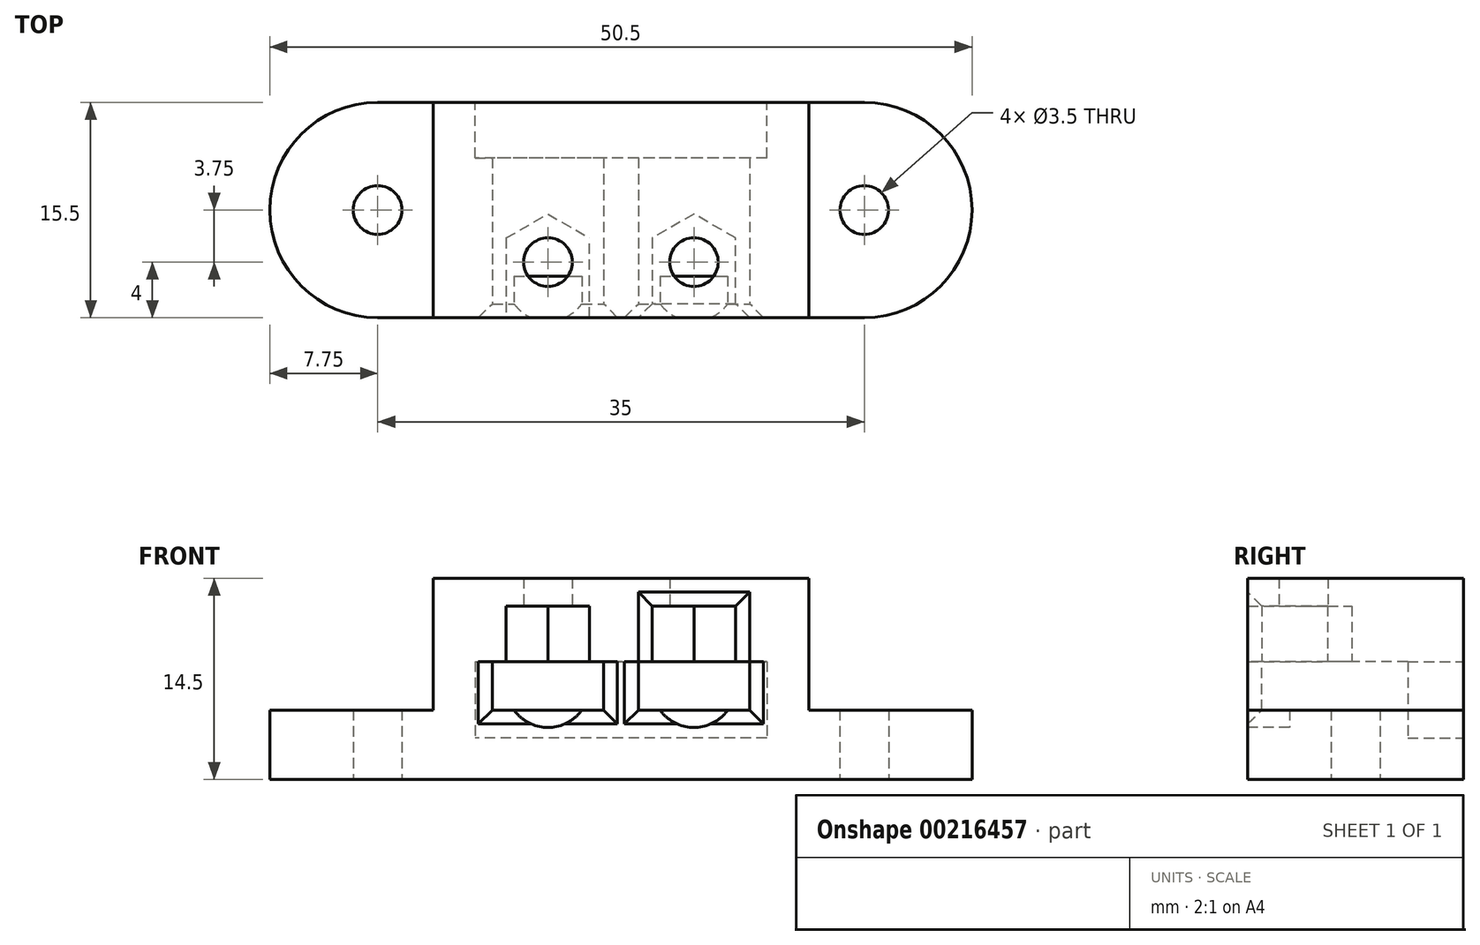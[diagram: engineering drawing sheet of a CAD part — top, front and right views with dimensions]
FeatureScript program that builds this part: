
annotation { "Feature Type Name" : "Feature", "Feature Type Description" : "" }
export const myFeature = defineFeature(function(context is Context, id is Id, definition is map)
    precondition{}
    {
        {
            var Q0;
            Q0=qCreatedBy(makeId("Top.planeOp"),FACE);
            var sketch = newSketch(context, id + "F0", { "sketchPlane" : qUnion([Q0])});
            skLineSegment(sketch, "E0", {"start": v(0, 0) * mm, "end": v(-1.25, 0) * mm});
            skLineSegment(sketch, "E1", {"start": v(-1.25, 0) * mm, "end": v(-1.25, -11.5) * mm});
            skLineSegment(sketch, "E2", {"start": v(-1.25, -11.5) * mm, "end": v(0, -11.5) * mm});
            skLineSegment(sketch, "E3", {"start": v(-5.25, 0) * mm, "end": v(-5.25, -13.93) * mm, "construction": true});
            skLineSegment(sketch, "E4.MirrorCS", {"start": v(-9.25, 0) * mm, "end": v(-9.25, -11.5) * mm});
            skLineSegment(sketch, "E5", {"start": v(-9.25, -11.5) * mm, "end": v(-10.5, -11.5) * mm});
            skLineSegment(sketch, "E6", {"start": v(-10.5, -11.5) * mm, "end": v(-10.5, 0) * mm});
            skLineSegment(sketch, "E7", {"start": v(-10.5, 0) * mm, "end": v(-9.25, 0) * mm});
            skLineSegment(sketch, "E8.MirrorCS", {"start": v(1.25, 0) * mm, "end": v(1.25, -11.5) * mm});
            skLineSegment(sketch, "E9.MirrorCS", {"start": v(1.25, -11.5) * mm, "end": v(0, -11.5) * mm});
            skLineSegment(sketch, "E10.MirrorCS", {"start": v(5.25, 0) * mm, "end": v(5.25, -13.93) * mm, "construction": true});
            skLineSegment(sketch, "E11.MirrorCS", {"start": v(9.25, -11.5) * mm, "end": v(10.5, -11.5) * mm});
            skLineSegment(sketch, "E12.MirrorCS", {"start": v(10.5, -11.5) * mm, "end": v(10.5, 0) * mm});
            skLineSegment(sketch, "E13.MirrorCS", {"start": v(10.5, 0) * mm, "end": v(9.25, 0) * mm});
            skLineSegment(sketch, "E14.MirrorCS", {"start": v(9.25, 0) * mm, "end": v(9.25, -11.5) * mm});
            skLineSegment(sketch, "E15.MirrorCS", {"start": v(0, 0) * mm, "end": v(1.25, 0) * mm});
            skSolve(sketch);
        }
        {
            var Q0;
            Q0=qSketchRegion(id+"F0",true);
            extrude(context, id + "F1", {"entities" : qUnion([Q0]), "depth" : 3.5 * mm});
        }
        {
            var Q0;
            Q0=qCreatedBy(makeId("Top.planeOp"),FACE);
            var sketch = newSketch(context, id + "F2", { "sketchPlane" : qUnion([Q0])});
            skLineSegment(sketch, "E16.bottom", {"start": v(10.5, 0) * mm, "end": v(-10.5, 0) * mm});
            skLineSegment(sketch, "E16.top", {"start": v(10.5, -11.5) * mm, "end": v(-10.5, -11.5) * mm});
            skLineSegment(sketch, "E16.left", {"start": v(10.5, 0) * mm, "end": v(10.5, -11.5) * mm});
            skLineSegment(sketch, "E16.right", {"start": v(-10.5, 0) * mm, "end": v(-10.5, -11.5) * mm});
            skSolve(sketch);
        }
        {
            var Q0;
            Q0=qSketchRegion(id+"F2",true);
            extrude(context, id + "F3", {"entities" : qUnion([Q0]), "operationType" : NewBodyOperationType.ADD, "oppositeDirection" : true, "depth" : 2 * mm});
        }
        {
            var Q0;
            Q0=qCreatedBy(makeId("Front.planeOp"),FACE);
            var sketch = newSketch(context, id + "F4", { "sketchPlane" : qUnion([Q0])});
            skLineSegment(sketch, "E17.bottom", {"start": v(-10.5, -2) * mm, "end": v(10.5, -2) * mm});
            skLineSegment(sketch, "E17.top", {"start": v(-10.5, 3.5) * mm, "end": v(10.5, 3.5) * mm});
            skLineSegment(sketch, "E17.left", {"start": v(-10.5, 3.5) * mm, "end": v(-10.5, -2) * mm});
            skLineSegment(sketch, "E17.right", {"start": v(10.5, 3.5) * mm, "end": v(10.5, -2) * mm});
            skLineSegment(sketch, "E18.bottom", {"start": v(-13.5, -5) * mm, "end": v(13.5, -5) * mm});
            skLineSegment(sketch, "E18.top", {"start": v(-13.5, 9.5) * mm, "end": v(13.5, 9.5) * mm});
            skLineSegment(sketch, "E18.left", {"start": v(-13.5, 9.5) * mm, "end": v(-13.5, -5) * mm});
            skLineSegment(sketch, "E18.right", {"start": v(13.5, 9.5) * mm, "end": v(13.5, -5) * mm});
            skPoint(sketch, "E19", {"position": v(0, -2) * mm});
            skPoint(sketch, "E20", {"position": v(0, -5) * mm});
            skPoint(sketch, "E21", {"position": v(10.5, 0.75) * mm});
            skSolve(sketch);
        }
        {
            var Q0;
            Q0 = qSketchRegion(id + "F4", true);
            var Q1;
            Q1=makeQuery(id+"F3.boolean.opBoolean","MERGE",FACE,{"derivedFrom":[makeQuery(id+"F1.opExtrude","SWEPT_FACE",FACE,{"disambiguationData":[OSD([sQuery(id+"F0.wireOp",EDGE,"E2"),sQuery(id+"F0.wireOp",EDGE,"E9.MirrorCS")])]}),makeQuery(id+"F1.opExtrude","SWEPT_FACE",FACE,{"disambiguationData":[OSD([sQuery(id+"F0.wireOp",EDGE,"E5")])]}),makeQuery(id+"F1.opExtrude","SWEPT_FACE",FACE,{"disambiguationData":[OSD([sQuery(id+"F0.wireOp",EDGE,"E11.MirrorCS")])]}),makeQuery(id+"F3.opExtrude","SWEPT_FACE",FACE,{"disambiguationData":[OSD([sQuery(id+"F2.wireOp",EDGE,"E16.top")])]})]});
            extrude(context, id + "F5", {"entities" : qUnion([Q0]), "operationType" : NewBodyOperationType.ADD, "endBound" : BoundingType.UP_TO_SURFACE, "endBoundEntityFace" : qUnion([Q1]), "depth" : 25 * mm, "hasSecondDirection" : true, "secondDirectionOppositeDirection" : true, "secondDirectionDepth" : 4 * mm});
        }
        {
            var Q0;
            {var subQ0=sQuery(id+"F2.wireOp",EDGE,"E16.bottom");var subQ1=sQuery(id+"F2.wireOp",EDGE,"E16.top");Q0=makeQuery(id+"F3.boolean.opBoolean","SPLIT",FACE,{"disambiguationData":[TD([makeQuery(id+"F1.opExtrude","SWEPT_FACE",FACE,{"disambiguationData":[OSD([sQuery(id+"F0.wireOp",EDGE,"E8.MirrorCS")])]})])],"derivedFrom":makeQuery(id+"F3.opExtrude","CAP_FACE",FACE,{"disambiguationData":[OSD([subQ0,subQ1,sQuery(id+"F2.wireOp",EDGE,"E16.left"),sQuery(id+"F2.wireOp",EDGE,"E16.right")])],"isStart":true})});}
            var sketch = newSketch(context, id + "F6", { "sketchPlane" : qUnion([Q0])});
            skCircle(sketch, "E22", {"center": v(5.25, -7.5) * mm, "radius": 1.75 * mm});
            skLineSegment(sketch, "E23", {"start": v(1.25, 0) * mm, "end": v(9.25, 0) * mm, "construction": true});
            skPoint(sketch, "E24", {"position": v(5.25, 0) * mm});
            skCircle(sketch, "E25.MirrorC", {"center": v(-5.25, -7.5) * mm, "radius": 1.75 * mm});
            skSolve(sketch);
        }
        {
            var Q0;
            Q0=qSketchRegion(id+"F6",true);
            extrude(context, id + "F7", {"entities" : qUnion([Q0]), "operationType" : NewBodyOperationType.REMOVE, "depth" : 25 * mm});
        }
        {
            var Q0;
            Q0=makeQuery(id+"F5.opExtrude","SWEPT_FACE",FACE,{"disambiguationData":[OSD([sQuery(id+"F4.wireOp",EDGE,"E17.top")])]});
            var sketch = newSketch(context, id + "F8", { "sketchPlane" : qUnion([Q0])});
            skCircle(sketch, "E26.cCircle", {"center": v(5.25, 7.5) * mm, "radius": 3 * mm, "construction": true});
            skLineSegment(sketch, "E26.0", {"start": v(5.25, 4.04) * mm, "end": v(2.25, 5.77) * mm});
            skLineSegment(sketch, "E26.1", {"start": v(2.25, 5.77) * mm, "end": v(2.25, 9.23) * mm});
            skLineSegment(sketch, "E26.2", {"start": v(2.25, 9.23) * mm, "end": v(5.25, 10.96) * mm});
            skLineSegment(sketch, "E26.3", {"start": v(5.25, 10.96) * mm, "end": v(8.25, 9.23) * mm});
            skLineSegment(sketch, "E26.4", {"start": v(8.25, 9.23) * mm, "end": v(8.25, 5.77) * mm});
            skLineSegment(sketch, "E26.5", {"start": v(8.25, 5.77) * mm, "end": v(5.25, 4.04) * mm});
            skPoint(sketch, "E26.0.midPoint", {"position": v(3.75, 4.9) * mm});
            skLineSegment(sketch, "E27", {"start": v(8.25, 9.23) * mm, "end": v(8.25, 21.02) * mm});
            skLineSegment(sketch, "E28", {"start": v(8.25, 21.02) * mm, "end": v(2.25, 21.02) * mm});
            skLineSegment(sketch, "E29", {"start": v(2.25, 21.02) * mm, "end": v(2.25, 9.23) * mm});
            skLineSegment(sketch, "E30.MirrorCS", {"start": v(-8.25, 21.02) * mm, "end": v(-2.25, 21.02) * mm});
            skLineSegment(sketch, "E31.MirrorCS", {"start": v(-2.25, 21.02) * mm, "end": v(-2.25, 9.23) * mm});
            skLineSegment(sketch, "E32.MirrorCS", {"start": v(-2.25, 5.77) * mm, "end": v(-2.25, 9.23) * mm});
            skLineSegment(sketch, "E33.MirrorCS", {"start": v(-5.25, 4.04) * mm, "end": v(-2.25, 5.77) * mm});
            skLineSegment(sketch, "E34.MirrorCS", {"start": v(-8.25, 5.77) * mm, "end": v(-5.25, 4.04) * mm});
            skLineSegment(sketch, "E35.MirrorCS", {"start": v(-8.25, 9.23) * mm, "end": v(-8.25, 5.77) * mm});
            skLineSegment(sketch, "E36.MirrorCS", {"start": v(-8.25, 9.23) * mm, "end": v(-8.25, 21.02) * mm});
            skSolve(sketch);
        }
        {
            var Q0;
            Q0=qSketchRegion(id+"F8",true);
            extrude(context, id + "F9", {"entities" : qUnion([Q0]), "operationType" : NewBodyOperationType.REMOVE, "oppositeDirection" : true, "depth" : 4 * mm});
        }
        {
            var Q0;
            {var subQ0=sQuery(id+"F2.wireOp",EDGE,"E16.top");var subQ1=sQuery(id+"F0.wireOp",EDGE,"E11.MirrorCS");var subQ2=sQuery(id+"F0.wireOp",EDGE,"E9.MirrorCS");var subQ3=sQuery(id+"F0.wireOp",EDGE,"E5");var subQ4=sQuery(id+"F0.wireOp",EDGE,"E2");Q0=makeQuery(id+"Fc77EeMiOFLoIx4_1.boolean.opBoolean","MERGE",FACE,{"derivedFrom":[makeQuery(id+"F3.boolean.opBoolean","MERGE",FACE,{"derivedFrom":[makeQuery(id+"F1.opExtrude","SWEPT_FACE",FACE,{"disambiguationData":[OSD([subQ4,subQ2])]}),makeQuery(id+"F1.opExtrude","SWEPT_FACE",FACE,{"disambiguationData":[OSD([subQ3])]}),makeQuery(id+"F1.opExtrude","SWEPT_FACE",FACE,{"disambiguationData":[OSD([subQ1])]}),makeQuery(id+"F3.opExtrude","SWEPT_FACE",FACE,{"disambiguationData":[OSD([subQ0])]})]}),makeQuery(id+"Fc77EeMiOFLoIx4_1.opExtrude","CAP_FACE",FACE,{"disambiguationData":[OSD([subQ4,subQ3,subQ2,subQ1,subQ0])],"isStart":true})]});}
            var sketch = newSketch(context, id + "F10", { "sketchPlane" : qUnion([Q0])});
            skPoint(sketch, "E37", {"position": v(9.25, 1.75) * mm});
            skPoint(sketch, "E38", {"position": v(5.25, 0) * mm});
            skCircle(sketch, "E39", {"center": v(5.25, 1.75) * mm, "radius": 3 * mm});
            skCircle(sketch, "E40.MirrorC", {"center": v(-5.25, 1.75) * mm, "radius": 3 * mm});
            skSolve(sketch);
        }
        {
            var Q0;
            Q0=qSketchRegion(id+"F10",true);
            extrude(context, id + "F11", {"entities" : qUnion([Q0]), "operationType" : NewBodyOperationType.REMOVE, "oppositeDirection" : true, "depth" : 3 * mm});
        }
        {
            var Q0;
            Q0=makeQuery(id+"F1.opExtrude","SWEPT_EDGE",EDGE,{"disambiguationData":[OSD([sQuery(id+"F0.wireOp",EDGE,"E1"),sQuery(id+"F0.wireOp",EDGE,"E2")])]});
            var Q1;
            {var subQ0=sQuery(id+"F0.wireOp",EDGE,"E11.MirrorCS");var subQ1=makeQuery(id+"F1.opExtrude","SWEPT_FACE",FACE,{"disambiguationData":[OSD([subQ0])]});var subQ2=sQuery(id+"F0.wireOp",EDGE,"E9.MirrorCS");var subQ3=sQuery(id+"F0.wireOp",EDGE,"E2");var subQ4=makeQuery(id+"F1.opExtrude","SWEPT_FACE",FACE,{"disambiguationData":[OSD([subQ3,subQ2])]});var subQ5=sQuery(id+"F0.wireOp",EDGE,"E5");var subQ6=makeQuery(id+"F1.opExtrude","SWEPT_FACE",FACE,{"disambiguationData":[OSD([subQ5])]});var subQ7=makeQuery(id+"F1.opExtrude","SWEPT_FACE",FACE,{"disambiguationData":[OSD([sQuery(id+"F0.wireOp",EDGE,"E1")])]});var subQ8=sQuery(id+"F2.wireOp",EDGE,"E16.top");var subQ9=makeQuery(id+"F3.opExtrude","SWEPT_FACE",FACE,{"disambiguationData":[OSD([subQ8])]});var subQ10=sQuery(id+"F4.wireOp",EDGE,"E17.top");Q1=makeQuery(id+"F9.boolean.opBoolean","SPLIT",EDGE,{"disambiguationData":[TD([subQ7])],"derivedFrom":makeQuery(id+"Fc77EeMiOFLoIx4_1.boolean.opBoolean","SPLIT",EDGE,{"disambiguationData":[TD([subQ7])],"derivedFrom":makeQuery(id+"Fc77EeMiOFLoIx4_1.opExtrude","TWEAK_EDGE",EDGE,{"derivedFrom":[makeQuery(id+"F3.boolean.opBoolean","MERGE",FACE,{"derivedFrom":[subQ4,subQ6,subQ1,subQ9]}),makeQuery(id+"F4.imprint","IMPRINT",EDGE,{"derivedFrom":subQ10})]})})});}
            var Q2;
            {var subQ0=sQuery(id+"F2.wireOp",EDGE,"E16.top");var subQ1=sQuery(id+"F0.wireOp",EDGE,"E11.MirrorCS");var subQ2=sQuery(id+"F0.wireOp",EDGE,"E9.MirrorCS");var subQ3=sQuery(id+"F0.wireOp",EDGE,"E5");var subQ4=sQuery(id+"F0.wireOp",EDGE,"E2");Q2=makeQuery(id+"F9.boolean.opBoolean","INTERSECT",EDGE,{"derivedFrom":[makeQuery(id+"Fc77EeMiOFLoIx4_1.boolean.opBoolean","MERGE",FACE,{"derivedFrom":[makeQuery(id+"F3.boolean.opBoolean","MERGE",FACE,{"derivedFrom":[makeQuery(id+"F1.opExtrude","SWEPT_FACE",FACE,{"disambiguationData":[OSD([subQ4,subQ2])]}),makeQuery(id+"F1.opExtrude","SWEPT_FACE",FACE,{"disambiguationData":[OSD([subQ3])]}),makeQuery(id+"F1.opExtrude","SWEPT_FACE",FACE,{"disambiguationData":[OSD([subQ1])]}),makeQuery(id+"F3.opExtrude","SWEPT_FACE",FACE,{"disambiguationData":[OSD([subQ0])]})]}),makeQuery(id+"Fc77EeMiOFLoIx4_1.opExtrude","CAP_FACE",FACE,{"disambiguationData":[OSD([subQ4,subQ3,subQ2,subQ1,subQ0])],"isStart":true})]}),makeQuery(id+"F9.opExtrude","SWEPT_FACE",FACE,{"disambiguationData":[OSD([sQuery(id+"F8.wireOp",EDGE,"E26.4"),sQuery(id+"F8.wireOp",EDGE,"E27")])]})]});}
            var Q3;
            {var subQ0=sQuery(id+"F2.wireOp",EDGE,"E16.top");var subQ1=sQuery(id+"F0.wireOp",EDGE,"E11.MirrorCS");var subQ2=sQuery(id+"F0.wireOp",EDGE,"E9.MirrorCS");var subQ3=sQuery(id+"F0.wireOp",EDGE,"E5");var subQ4=sQuery(id+"F0.wireOp",EDGE,"E2");Q3=makeQuery(id+"F9.boolean.opBoolean","INTERSECT",EDGE,{"derivedFrom":[makeQuery(id+"Fc77EeMiOFLoIx4_1.boolean.opBoolean","MERGE",FACE,{"derivedFrom":[makeQuery(id+"F3.boolean.opBoolean","MERGE",FACE,{"derivedFrom":[makeQuery(id+"F1.opExtrude","SWEPT_FACE",FACE,{"disambiguationData":[OSD([subQ4,subQ2])]}),makeQuery(id+"F1.opExtrude","SWEPT_FACE",FACE,{"disambiguationData":[OSD([subQ3])]}),makeQuery(id+"F1.opExtrude","SWEPT_FACE",FACE,{"disambiguationData":[OSD([subQ1])]}),makeQuery(id+"F3.opExtrude","SWEPT_FACE",FACE,{"disambiguationData":[OSD([subQ0])]})]}),makeQuery(id+"Fc77EeMiOFLoIx4_1.opExtrude","CAP_FACE",FACE,{"disambiguationData":[OSD([subQ4,subQ3,subQ2,subQ1,subQ0])],"isStart":true})]}),makeQuery(id+"F9.opExtrude","CAP_FACE",FACE,{"disambiguationData":[OSD([sQuery(id+"F8.wireOp",EDGE,"E26.0"),sQuery(id+"F8.wireOp",EDGE,"E26.1"),sQuery(id+"F8.wireOp",EDGE,"E26.4"),sQuery(id+"F8.wireOp",EDGE,"E26.5"),sQuery(id+"F8.wireOp",EDGE,"E27"),sQuery(id+"F8.wireOp",EDGE,"E28"),sQuery(id+"F8.wireOp",EDGE,"E29")])],"isStart":false})]});}
            var Q4;
            {var subQ0=sQuery(id+"F2.wireOp",EDGE,"E16.top");var subQ1=sQuery(id+"F0.wireOp",EDGE,"E11.MirrorCS");var subQ2=sQuery(id+"F0.wireOp",EDGE,"E9.MirrorCS");var subQ3=sQuery(id+"F0.wireOp",EDGE,"E5");var subQ4=sQuery(id+"F0.wireOp",EDGE,"E2");Q4=makeQuery(id+"F9.boolean.opBoolean","INTERSECT",EDGE,{"derivedFrom":[makeQuery(id+"Fc77EeMiOFLoIx4_1.boolean.opBoolean","MERGE",FACE,{"derivedFrom":[makeQuery(id+"F3.boolean.opBoolean","MERGE",FACE,{"derivedFrom":[makeQuery(id+"F1.opExtrude","SWEPT_FACE",FACE,{"disambiguationData":[OSD([subQ4,subQ2])]}),makeQuery(id+"F1.opExtrude","SWEPT_FACE",FACE,{"disambiguationData":[OSD([subQ3])]}),makeQuery(id+"F1.opExtrude","SWEPT_FACE",FACE,{"disambiguationData":[OSD([subQ1])]}),makeQuery(id+"F3.opExtrude","SWEPT_FACE",FACE,{"disambiguationData":[OSD([subQ0])]})]}),makeQuery(id+"Fc77EeMiOFLoIx4_1.opExtrude","CAP_FACE",FACE,{"disambiguationData":[OSD([subQ4,subQ3,subQ2,subQ1,subQ0])],"isStart":true})]}),makeQuery(id+"F9.opExtrude","SWEPT_FACE",FACE,{"disambiguationData":[OSD([sQuery(id+"F8.wireOp",EDGE,"E26.1"),sQuery(id+"F8.wireOp",EDGE,"E29")])]})]});}
            var Q5;
            {var subQ0=sQuery(id+"F0.wireOp",EDGE,"E11.MirrorCS");var subQ1=makeQuery(id+"F1.opExtrude","SWEPT_FACE",FACE,{"disambiguationData":[OSD([subQ0])]});var subQ2=makeQuery(id+"F1.opExtrude","SWEPT_FACE",FACE,{"disambiguationData":[OSD([sQuery(id+"F0.wireOp",EDGE,"E4.MirrorCS")])]});var subQ3=sQuery(id+"F0.wireOp",EDGE,"E5");var subQ4=makeQuery(id+"F1.opExtrude","SWEPT_FACE",FACE,{"disambiguationData":[OSD([subQ3])]});var subQ5=sQuery(id+"F0.wireOp",EDGE,"E9.MirrorCS");var subQ6=sQuery(id+"F0.wireOp",EDGE,"E2");var subQ7=makeQuery(id+"F1.opExtrude","SWEPT_FACE",FACE,{"disambiguationData":[OSD([subQ6,subQ5])]});var subQ8=sQuery(id+"F2.wireOp",EDGE,"E16.top");var subQ9=makeQuery(id+"F3.opExtrude","SWEPT_FACE",FACE,{"disambiguationData":[OSD([subQ8])]});var subQ10=sQuery(id+"F4.wireOp",EDGE,"E17.top");Q5=makeQuery(id+"F9.boolean.opBoolean","SPLIT",EDGE,{"disambiguationData":[TD([subQ2])],"derivedFrom":makeQuery(id+"Fc77EeMiOFLoIx4_1.boolean.opBoolean","SPLIT",EDGE,{"disambiguationData":[TD([makeQuery(id+"F1.opExtrude","SWEPT_FACE",FACE,{"disambiguationData":[OSD([sQuery(id+"F0.wireOp",EDGE,"E1")])]})])],"derivedFrom":makeQuery(id+"Fc77EeMiOFLoIx4_1.opExtrude","TWEAK_EDGE",EDGE,{"derivedFrom":[makeQuery(id+"F3.boolean.opBoolean","MERGE",FACE,{"derivedFrom":[subQ7,subQ4,subQ1,subQ9]}),makeQuery(id+"F4.imprint","IMPRINT",EDGE,{"derivedFrom":subQ10})]})})});}
            var Q6;
            Q6=makeQuery(id+"F1.opExtrude","SWEPT_EDGE",EDGE,{"disambiguationData":[OSD([sQuery(id+"F0.wireOp",EDGE,"E4.MirrorCS"),sQuery(id+"F0.wireOp",EDGE,"E5")])]});
            var Q7;
            {var subQ0=sQuery(id+"F2.wireOp",EDGE,"E16.top");Q7=makeQuery(id+"F3.boolean.opBoolean","SPLIT",EDGE,{"disambiguationData":[TD([makeQuery(id+"F1.opExtrude","SWEPT_FACE",FACE,{"disambiguationData":[OSD([sQuery(id+"F0.wireOp",EDGE,"E1")])]})])],"derivedFrom":makeQuery(id+"F3.opExtrude","CAP_EDGE",EDGE,{"disambiguationData":[OSD([subQ0])],"isStart":true})});}
            var Q8;
            {var subQ2=makeQuery(id+"F1.opExtrude","SWEPT_FACE",FACE,{"disambiguationData":[OSD([sQuery(id+"F0.wireOp",EDGE,"E8.MirrorCS")])]});var subQ8=sQuery(id+"F2.wireOp",EDGE,"E16.top");Q8=makeQuery(id+"F11.boolean.opBoolean","SPLIT",EDGE,{"disambiguationData":[TD([subQ2])],"derivedFrom":makeQuery(id+"F3.boolean.opBoolean","SPLIT",EDGE,{"disambiguationData":[TD([subQ2])],"derivedFrom":makeQuery(id+"F3.opExtrude","CAP_EDGE",EDGE,{"disambiguationData":[OSD([subQ8])],"isStart":true})})});}
            var Q9;
            Q9=makeQuery(id+"F1.opExtrude","SWEPT_EDGE",EDGE,{"disambiguationData":[OSD([sQuery(id+"F0.wireOp",EDGE,"E8.MirrorCS"),sQuery(id+"F0.wireOp",EDGE,"E9.MirrorCS")])]});
            var Q10;
            Q10=makeQuery(id+"F11.boolean.opBoolean","COPY",EDGE,{"derivedFrom":makeQuery(id+"F11.opExtrude","CAP_EDGE",EDGE,{"disambiguationData":[OSD([sQuery(id+"F10.wireOp",EDGE,"E39")])],"isStart":true})});
            var Q11;
            {var subQ2=makeQuery(id+"F1.opExtrude","SWEPT_FACE",FACE,{"disambiguationData":[OSD([sQuery(id+"F0.wireOp",EDGE,"E14.MirrorCS")])]});var subQ8=sQuery(id+"F2.wireOp",EDGE,"E16.top");Q11=makeQuery(id+"F11.boolean.opBoolean","SPLIT",EDGE,{"disambiguationData":[TD([subQ2])],"derivedFrom":makeQuery(id+"F3.boolean.opBoolean","SPLIT",EDGE,{"disambiguationData":[TD([makeQuery(id+"F1.opExtrude","SWEPT_FACE",FACE,{"disambiguationData":[OSD([sQuery(id+"F0.wireOp",EDGE,"E8.MirrorCS")])]})])],"derivedFrom":makeQuery(id+"F3.opExtrude","CAP_EDGE",EDGE,{"disambiguationData":[OSD([subQ8])],"isStart":true})})});}
            var Q12;
            Q12=makeQuery(id+"F1.opExtrude","SWEPT_EDGE",EDGE,{"disambiguationData":[OSD([sQuery(id+"F0.wireOp",EDGE,"E11.MirrorCS"),sQuery(id+"F0.wireOp",EDGE,"E14.MirrorCS")])]});
            var Q13;
            {var subQ0=sQuery(id+"F0.wireOp",EDGE,"E11.MirrorCS");var subQ1=makeQuery(id+"F1.opExtrude","SWEPT_FACE",FACE,{"disambiguationData":[OSD([subQ0])]});var subQ2=makeQuery(id+"F1.opExtrude","SWEPT_FACE",FACE,{"disambiguationData":[OSD([sQuery(id+"F0.wireOp",EDGE,"E14.MirrorCS")])]});var subQ3=sQuery(id+"F0.wireOp",EDGE,"E5");var subQ4=makeQuery(id+"F1.opExtrude","SWEPT_FACE",FACE,{"disambiguationData":[OSD([subQ3])]});var subQ5=sQuery(id+"F0.wireOp",EDGE,"E9.MirrorCS");var subQ6=sQuery(id+"F0.wireOp",EDGE,"E2");var subQ7=makeQuery(id+"F1.opExtrude","SWEPT_FACE",FACE,{"disambiguationData":[OSD([subQ6,subQ5])]});var subQ8=sQuery(id+"F2.wireOp",EDGE,"E16.top");var subQ9=makeQuery(id+"F3.opExtrude","SWEPT_FACE",FACE,{"disambiguationData":[OSD([subQ8])]});var subQ10=sQuery(id+"F4.wireOp",EDGE,"E17.top");Q13=makeQuery(id+"F9.boolean.opBoolean","SPLIT",EDGE,{"disambiguationData":[TD([subQ2])],"derivedFrom":makeQuery(id+"Fc77EeMiOFLoIx4_1.boolean.opBoolean","SPLIT",EDGE,{"disambiguationData":[TD([makeQuery(id+"F1.opExtrude","SWEPT_FACE",FACE,{"disambiguationData":[OSD([sQuery(id+"F0.wireOp",EDGE,"E8.MirrorCS")])]})])],"derivedFrom":makeQuery(id+"Fc77EeMiOFLoIx4_1.opExtrude","TWEAK_EDGE",EDGE,{"derivedFrom":[makeQuery(id+"F3.boolean.opBoolean","MERGE",FACE,{"derivedFrom":[subQ7,subQ4,subQ1,subQ9]}),makeQuery(id+"F4.imprint","IMPRINT",EDGE,{"derivedFrom":subQ10})]})})});}
            var Q14;
            {var subQ0=sQuery(id+"F2.wireOp",EDGE,"E16.top");var subQ1=sQuery(id+"F0.wireOp",EDGE,"E11.MirrorCS");var subQ2=sQuery(id+"F0.wireOp",EDGE,"E9.MirrorCS");var subQ3=sQuery(id+"F0.wireOp",EDGE,"E5");var subQ4=sQuery(id+"F0.wireOp",EDGE,"E2");Q14=makeQuery(id+"F9.boolean.opBoolean","INTERSECT",EDGE,{"derivedFrom":[makeQuery(id+"Fc77EeMiOFLoIx4_1.boolean.opBoolean","MERGE",FACE,{"derivedFrom":[makeQuery(id+"F3.boolean.opBoolean","MERGE",FACE,{"derivedFrom":[makeQuery(id+"F1.opExtrude","SWEPT_FACE",FACE,{"disambiguationData":[OSD([subQ4,subQ2])]}),makeQuery(id+"F1.opExtrude","SWEPT_FACE",FACE,{"disambiguationData":[OSD([subQ3])]}),makeQuery(id+"F1.opExtrude","SWEPT_FACE",FACE,{"disambiguationData":[OSD([subQ1])]}),makeQuery(id+"F3.opExtrude","SWEPT_FACE",FACE,{"disambiguationData":[OSD([subQ0])]})]}),makeQuery(id+"Fc77EeMiOFLoIx4_1.opExtrude","CAP_FACE",FACE,{"disambiguationData":[OSD([subQ4,subQ3,subQ2,subQ1,subQ0])],"isStart":true})]}),makeQuery(id+"F9.opExtrude","SWEPT_FACE",FACE,{"disambiguationData":[OSD([sQuery(id+"F8.wireOp",EDGE,"bf6aa4e6-f689-4d3c-bee1-64649f7bd7840.MirrorCS"),sQuery(id+"F8.wireOp",EDGE,"ed661a8c-ccfc-44a2-91c2-af6a565475d80.MirrorCS")])]})]});}
            var Q15;
            {var subQ0=sQuery(id+"F2.wireOp",EDGE,"E16.top");var subQ1=sQuery(id+"F0.wireOp",EDGE,"E11.MirrorCS");var subQ2=sQuery(id+"F0.wireOp",EDGE,"E9.MirrorCS");var subQ3=sQuery(id+"F0.wireOp",EDGE,"E5");var subQ4=sQuery(id+"F0.wireOp",EDGE,"E2");Q15=makeQuery(id+"F9.boolean.opBoolean","INTERSECT",EDGE,{"derivedFrom":[makeQuery(id+"Fc77EeMiOFLoIx4_1.boolean.opBoolean","MERGE",FACE,{"derivedFrom":[makeQuery(id+"F3.boolean.opBoolean","MERGE",FACE,{"derivedFrom":[makeQuery(id+"F1.opExtrude","SWEPT_FACE",FACE,{"disambiguationData":[OSD([subQ4,subQ2])]}),makeQuery(id+"F1.opExtrude","SWEPT_FACE",FACE,{"disambiguationData":[OSD([subQ3])]}),makeQuery(id+"F1.opExtrude","SWEPT_FACE",FACE,{"disambiguationData":[OSD([subQ1])]}),makeQuery(id+"F3.opExtrude","SWEPT_FACE",FACE,{"disambiguationData":[OSD([subQ0])]})]}),makeQuery(id+"Fc77EeMiOFLoIx4_1.opExtrude","CAP_FACE",FACE,{"disambiguationData":[OSD([subQ4,subQ3,subQ2,subQ1,subQ0])],"isStart":true})]}),makeQuery(id+"F9.opExtrude","CAP_FACE",FACE,{"disambiguationData":[OSD([sQuery(id+"F8.wireOp",EDGE,"667f863f-4758-48ef-aaf0-df25e78e16a60.MirrorCS"),sQuery(id+"F8.wireOp",EDGE,"55b3d782-bdb8-4c63-9c4a-2ec13156e9610.MirrorCS"),sQuery(id+"F8.wireOp",EDGE,"e81c9eea-3ff5-49a1-ab79-a9152e500f9e0.MirrorCS"),sQuery(id+"F8.wireOp",EDGE,"5bf6942d-2026-454f-845e-f4a78c062d0b0.MirrorCS"),sQuery(id+"F8.wireOp",EDGE,"bf6aa4e6-f689-4d3c-bee1-64649f7bd7840.MirrorCS"),sQuery(id+"F8.wireOp",EDGE,"ed661a8c-ccfc-44a2-91c2-af6a565475d80.MirrorCS"),sQuery(id+"F8.wireOp",EDGE,"8dd25266-44c5-4174-91cd-92a5649f7e610.MirrorCS")])],"isStart":false})]});}
            var Q16;
            {var subQ0=sQuery(id+"F2.wireOp",EDGE,"E16.top");var subQ1=sQuery(id+"F0.wireOp",EDGE,"E11.MirrorCS");var subQ2=sQuery(id+"F0.wireOp",EDGE,"E9.MirrorCS");var subQ3=sQuery(id+"F0.wireOp",EDGE,"E5");var subQ4=sQuery(id+"F0.wireOp",EDGE,"E2");Q16=makeQuery(id+"F9.boolean.opBoolean","INTERSECT",EDGE,{"derivedFrom":[makeQuery(id+"Fc77EeMiOFLoIx4_1.boolean.opBoolean","MERGE",FACE,{"derivedFrom":[makeQuery(id+"F3.boolean.opBoolean","MERGE",FACE,{"derivedFrom":[makeQuery(id+"F1.opExtrude","SWEPT_FACE",FACE,{"disambiguationData":[OSD([subQ4,subQ2])]}),makeQuery(id+"F1.opExtrude","SWEPT_FACE",FACE,{"disambiguationData":[OSD([subQ3])]}),makeQuery(id+"F1.opExtrude","SWEPT_FACE",FACE,{"disambiguationData":[OSD([subQ1])]}),makeQuery(id+"F3.opExtrude","SWEPT_FACE",FACE,{"disambiguationData":[OSD([subQ0])]})]}),makeQuery(id+"Fc77EeMiOFLoIx4_1.opExtrude","CAP_FACE",FACE,{"disambiguationData":[OSD([subQ4,subQ3,subQ2,subQ1,subQ0])],"isStart":true})]}),makeQuery(id+"F9.opExtrude","SWEPT_FACE",FACE,{"disambiguationData":[OSD([sQuery(id+"F8.wireOp",EDGE,"55b3d782-bdb8-4c63-9c4a-2ec13156e9610.MirrorCS"),sQuery(id+"F8.wireOp",EDGE,"e81c9eea-3ff5-49a1-ab79-a9152e500f9e0.MirrorCS")])]})]});}
            var Q17;
            {var subQ0=sQuery(id+"F0.wireOp",EDGE,"E11.MirrorCS");var subQ1=makeQuery(id+"F1.opExtrude","SWEPT_FACE",FACE,{"disambiguationData":[OSD([subQ0])]});var subQ2=makeQuery(id+"F1.opExtrude","SWEPT_FACE",FACE,{"disambiguationData":[OSD([sQuery(id+"F0.wireOp",EDGE,"E8.MirrorCS")])]});var subQ3=sQuery(id+"F0.wireOp",EDGE,"E5");var subQ4=makeQuery(id+"F1.opExtrude","SWEPT_FACE",FACE,{"disambiguationData":[OSD([subQ3])]});var subQ5=sQuery(id+"F0.wireOp",EDGE,"E9.MirrorCS");var subQ6=sQuery(id+"F0.wireOp",EDGE,"E2");var subQ7=makeQuery(id+"F1.opExtrude","SWEPT_FACE",FACE,{"disambiguationData":[OSD([subQ6,subQ5])]});var subQ8=sQuery(id+"F2.wireOp",EDGE,"E16.top");var subQ9=makeQuery(id+"F3.opExtrude","SWEPT_FACE",FACE,{"disambiguationData":[OSD([subQ8])]});var subQ10=sQuery(id+"F4.wireOp",EDGE,"E17.top");Q17=makeQuery(id+"F9.boolean.opBoolean","SPLIT",EDGE,{"disambiguationData":[TD([subQ2])],"derivedFrom":makeQuery(id+"Fc77EeMiOFLoIx4_1.boolean.opBoolean","SPLIT",EDGE,{"disambiguationData":[TD([subQ2])],"derivedFrom":makeQuery(id+"Fc77EeMiOFLoIx4_1.opExtrude","TWEAK_EDGE",EDGE,{"derivedFrom":[makeQuery(id+"F3.boolean.opBoolean","MERGE",FACE,{"derivedFrom":[subQ7,subQ4,subQ1,subQ9]}),makeQuery(id+"F4.imprint","IMPRINT",EDGE,{"derivedFrom":subQ10})]})})});}
            var Q18;
            Q18=makeQuery(id+"F11.boolean.opBoolean","COPY",EDGE,{"derivedFrom":makeQuery(id+"F11.opExtrude","CAP_EDGE",EDGE,{"disambiguationData":[OSD([sQuery(id+"F10.wireOp",EDGE,"E40.MirrorC")])],"isStart":true})});
            chamfer(context, id + "F12", {"entities" : qUnion([Q0, Q1, Q2, Q3, Q4, Q5, Q6, Q7, Q8, Q9, Q10, Q11, Q12, Q13, Q14, Q15, Q16, Q17, Q18]), "width" : 1 * mm, "tangentPropagation" : true});
        }
        {
            var Q0;
            Q0=makeQuery(id+"F5.opExtrude","SWEPT_FACE",FACE,{"disambiguationData":[OSD([sQuery(id+"F4.wireOp",EDGE,"E18.bottom")])]});
            var sketch = newSketch(context, id + "F13", { "sketchPlane" : qUnion([Q0])});
            skArc(sketch, "E41", {"start": v(17.5, -4) * mm, "mid": v(25.25, 3.75) * mm, "end": v(17.5, 11.5) * mm});
            skCircle(sketch, "E42", {"center": v(17.5, 3.75) * mm, "radius": 1.75 * mm});
            skArc(sketch, "E43.MirrorCS", {"start": v(-17.5, -4) * mm, "mid": v(-25.25, 3.75) * mm, "end": v(-17.5, 11.5) * mm});
            skCircle(sketch, "E44.MirrorC", {"center": v(-17.5, 3.75) * mm, "radius": 1.75 * mm});
            skLineSegment(sketch, "E45", {"start": v(-17.5, 11.5) * mm, "end": v(-13.5, 11.5) * mm});
            skLineSegment(sketch, "E46", {"start": v(17.5, -4) * mm, "end": v(13.5, -4) * mm});
            skLineSegment(sketch, "E47", {"start": v(-13.5, 11.5) * mm, "end": v(-13.5, -4) * mm});
            skLineSegment(sketch, "E48", {"start": v(13.5, 11.5) * mm, "end": v(13.5, -4) * mm});
            skLineSegment(sketch, "E49.trimOffspring", {"start": v(13.5, 11.5) * mm, "end": v(17.5, 11.5) * mm});
            skLineSegment(sketch, "E50.trimOffspring", {"start": v(-13.5, -4) * mm, "end": v(-17.5, -4) * mm});
            skSolve(sketch);
        }
        {
            var Q0;
            Q0 = qSketchRegion(id + "F13", true);
            extrude(context, id + "F14", {"entities" : qUnion([Q0]), "operationType" : NewBodyOperationType.ADD, "oppositeDirection" : true, "depth" : 5 * mm});
        }
    });
